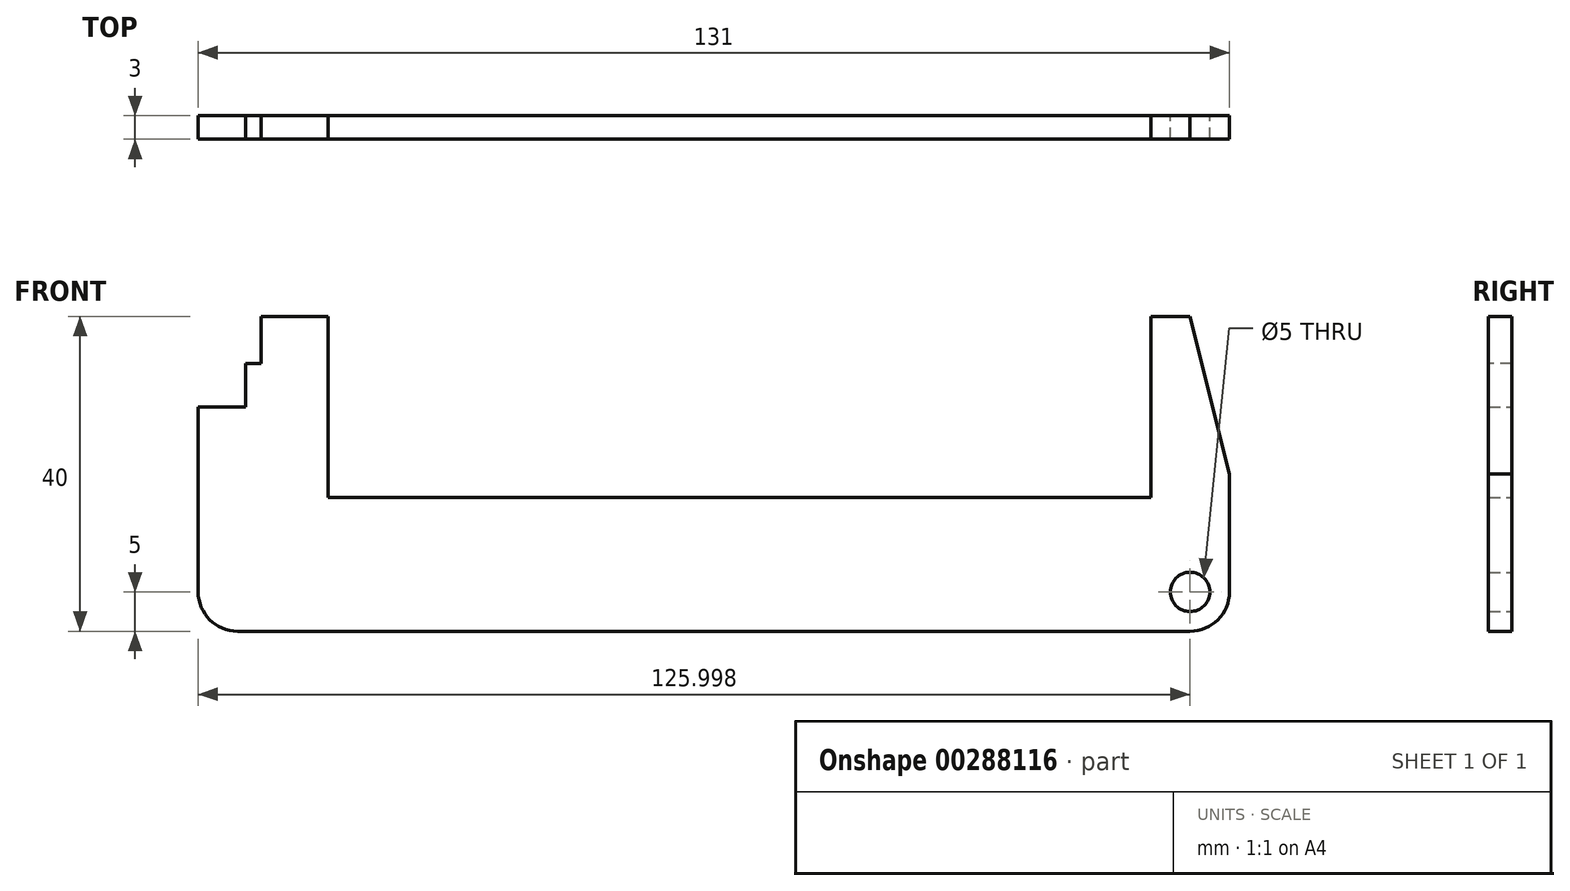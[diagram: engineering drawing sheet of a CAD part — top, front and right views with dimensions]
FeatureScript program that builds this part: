
annotation { "Feature Type Name" : "Feature", "Feature Type Description" : "" }
export const myFeature = defineFeature(function(context is Context, id is Id, definition is map)
    precondition{}
    {
        {
            var Q0;
            Q0=qCreatedBy(makeId("Front.planeOp"),FACE);
            var sketch = newSketch(context, id + "F0", { "sketchPlane" : qUnion([Q0])});
            skLineSegment(sketch, "E0", {"start": v(-65.77, 28.5) * mm, "end": v(-59.77, 28.5) * mm});
            skLineSegment(sketch, "E1", {"start": v(-59.77, 28.5) * mm, "end": v(-59.77, 40) * mm});
            skLineSegment(sketch, "E2", {"start": v(-59.77, 40) * mm, "end": v(-49.27, 40) * mm});
            skLineSegment(sketch, "E3", {"start": v(-49.27, 40) * mm, "end": v(-49.27, 17) * mm});
            skLineSegment(sketch, "E4", {"start": v(-49.27, 17) * mm, "end": v(55.23, 17) * mm});
            skLineSegment(sketch, "E5", {"start": v(55.23, 17) * mm, "end": v(55.23, 40) * mm});
            skLineSegment(sketch, "E6", {"start": v(55.23, 40) * mm, "end": v(60.23, 40) * mm});
            skLineSegment(sketch, "E7", {"start": v(60.23, 40) * mm, "end": v(65.23, 20) * mm});
            skCircle(sketch, "E8", {"center": v(60.23, 5) * mm, "radius": 2.5 * mm});
            skLineSegment(sketch, "E9", {"start": v(65.23, 20) * mm, "end": v(65.23, 5) * mm});
            skLineSegment(sketch, "E10", {"start": v(-65.77, 28.5) * mm, "end": v(-65.77, 5) * mm});
            skLineSegment(sketch, "E11", {"start": v(60.23, 0) * mm, "end": v(-60.77, 0) * mm});
            skArc(sketch, "E12", {"start": v(-65.77, 5) * mm, "mid": v(-64.3, 1.46) * mm, "end": v(-60.77, 0) * mm});
            skArc(sketch, "E13", {"start": v(60.23, 0) * mm, "mid": v(63.76, 1.46) * mm, "end": v(65.23, 5) * mm});
            skSolve(sketch);
        }
        {
            var Q0;
            Q0=makeQuery(id+"F0.imprint","IMPRINT",FACE,{"disambiguationData":[TD([[makeQuery(id+"F0.imprint","IMPRINT",EDGE,{"derivedFrom":sQuery(id+"F0.wireOp",EDGE,"E0")}),-1.0]])]});
            extrude(context, id + "F1", {"entities" : qUnion([Q0]), "depth" : 3 * mm});
        }
        {
            var Q0;
            Q0=makeQuery(id+"F1.opExtrude","CAP_FACE",FACE,{"disambiguationData":[OSD([sQuery(id+"F0.wireOp",EDGE,"E0"),sQuery(id+"F0.wireOp",EDGE,"E1"),sQuery(id+"F0.wireOp",EDGE,"E2"),sQuery(id+"F0.wireOp",EDGE,"E3"),sQuery(id+"F0.wireOp",EDGE,"E4"),sQuery(id+"F0.wireOp",EDGE,"E5"),sQuery(id+"F0.wireOp",EDGE,"E6"),sQuery(id+"F0.wireOp",EDGE,"E7"),sQuery(id+"F0.wireOp",EDGE,"E8"),sQuery(id+"F0.wireOp",EDGE,"E9"),sQuery(id+"F0.wireOp",EDGE,"E10"),sQuery(id+"F0.wireOp",EDGE,"E11"),sQuery(id+"F0.wireOp",EDGE,"E12"),sQuery(id+"F0.wireOp",EDGE,"E13")])],"isStart":false});
            var sketch = newSketch(context, id + "F2", { "sketchPlane" : qUnion([Q0])});
            skLineSegment(sketch, "E14.bottom", {"start": v(-59.77, 40) * mm, "end": v(-57.77, 40) * mm});
            skLineSegment(sketch, "E14.top", {"start": v(-59.77, 34) * mm, "end": v(-57.77, 34) * mm});
            skLineSegment(sketch, "E14.left", {"start": v(-59.77, 40) * mm, "end": v(-59.77, 34) * mm});
            skLineSegment(sketch, "E14.right", {"start": v(-57.77, 40) * mm, "end": v(-57.77, 34) * mm});
            skSolve(sketch);
        }
        {
            var Q0;
            Q0=makeQuery(id+"F2.imprint","IMPRINT",FACE,{"disambiguationData":[TD([[makeQuery(id+"F2.imprint","IMPRINT",EDGE,{"derivedFrom":sQuery(id+"F2.wireOp",EDGE,"E14.bottom")}),-1.0]])]});
            extrude(context, id + "F3", {"entities" : qUnion([Q0]), "operationType" : NewBodyOperationType.REMOVE, "endBound" : BoundingType.THROUGH_ALL, "oppositeDirection" : true, "depth" : 25 * mm, "offsetDistance" : 25 * mm});
        }
    });
